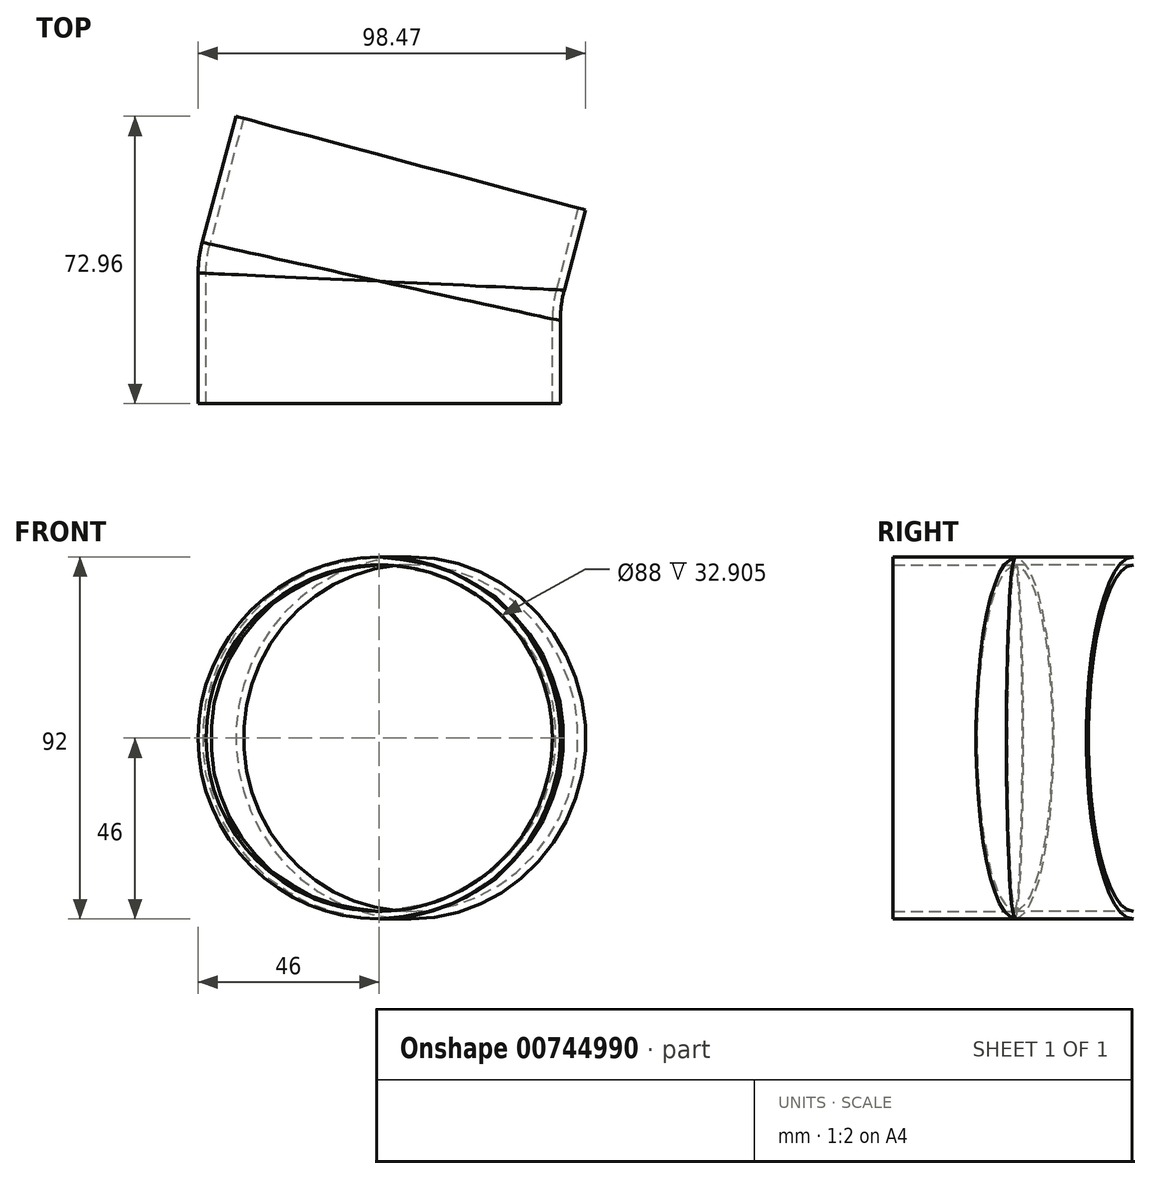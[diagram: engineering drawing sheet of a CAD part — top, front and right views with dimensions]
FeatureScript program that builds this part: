
annotation { "Feature Type Name" : "Feature", "Feature Type Description" : "" }
export const myFeature = defineFeature(function(context is Context, id is Id, definition is map)
    precondition{}
    {
        {
            var Q0;
            Q0=qCreatedBy(makeId("Front.planeOp"),FACE);
            var sketch = newSketch(context, id + "F0", { "sketchPlane" : qUnion([Q0])});
            skCircle(sketch, "E0", {"center": v(0, 0) * mm, "radius": 46 * mm});
            skSolve(sketch);
        }
        {
            var Q0;
            Q0=makeQuery(id+"F0.imprint","IMPRINT",FACE,{"disambiguationData":[TD([[makeQuery(id+"F0.imprint","IMPRINT",EDGE,{"derivedFrom":sQuery(id+"F0.wireOp",EDGE,"E0")}),1.0]])]});
            extrude(context, id + "F1", {"entities" : qUnion([Q0]), "depth" : 50 * mm, "offsetDistance" : 25 * mm});
        }
        {
            var Q0;
            Q0=qCreatedBy(makeId("Top.planeOp"),FACE);
            var sketch = newSketch(context, id + "F2", { "sketchPlane" : qUnion([Q0])});
            skLineSegment(sketch, "E1", {"start": v(0, 0) * mm, "end": v(46, 0) * mm, "construction": true});
            skLineSegment(sketch, "E2", {"start": v(46, 0) * mm, "end": v(-46, 0) * mm});
            skLineSegment(sketch, "E3", {"start": v(-46, 0) * mm, "end": v(-46, -12.89) * mm});
            skLineSegment(sketch, "E4", {"start": v(46, 0) * mm, "end": v(46, -25) * mm});
            skLineSegment(sketch, "E5", {"start": v(46, -25) * mm, "end": v(-46, -12.89) * mm});
            skSolve(sketch);
        }
        {
            var Q0;
            Q0 = qSketchRegion(id + "F2", true);
            extrude(context, id + "F3", {"entities" : qUnion([Q0]), "operationType" : NewBodyOperationType.REMOVE, "endBound" : BoundingType.THROUGH_ALL, "oppositeDirection" : true, "depth" : 25 * mm, "offsetDistance" : 25 * mm, "hasSecondDirection" : true, "secondDirectionBound" : SecondDirectionBoundingType.THROUGH_ALL, "secondDirectionOppositeDirection" : false, "secondDirectionDepth" : 25 * mm});
        }
        {
            var Q0;
            Q0=qCreatedBy(makeId("Front.planeOp"),FACE);
            var sketch = newSketch(context, id + "F4", { "sketchPlane" : qUnion([Q0])});
            skCircle(sketch, "E6", {"center": v(0, 0) * mm, "radius": 44 * mm});
            skSolve(sketch);
        }
        {
            var Q0;
            Q0 = qSketchRegion(id + "F4", true);
            extrude(context, id + "F5", {"entities" : qUnion([Q0]), "operationType" : NewBodyOperationType.REMOVE, "endBound" : BoundingType.THROUGH_ALL, "depth" : 25 * mm, "offsetDistance" : 25 * mm});
        }
        {
            var Q0;
            Q0=makeQuery(id+"F1.opExtrude","SWEPT_BODY",BODY,{"disambiguationData":[OSD([sQuery(id+"F0.wireOp",EDGE,"E0")])]});
            var Q1;
            Q1=makeQuery(id+"F3.boolean.opBoolean","COPY",FACE,{"derivedFrom":makeQuery(id+"F3.opExtrude","SWEPT_FACE",FACE,{"disambiguationData":[OSD([sQuery(id+"F2.wireOp",EDGE,"E5")])]})});
            mirror(context, id + "F6", {"operationType" : NewBodyOperationType.ADD, "entities" : qUnion([Q0]), "mirrorPlane" : qUnion([Q1])});
        }
        {
            var Q0;
            {var subQ0=makeQuery(id+"F5.boolean.opBoolean","INTERSECT",EDGE,{"derivedFrom":[makeQuery(id+"F3.boolean.opBoolean","COPY",FACE,{"derivedFrom":makeQuery(id+"F3.opExtrude","SWEPT_FACE",FACE,{"disambiguationData":[OSD([sQuery(id+"F2.wireOp",EDGE,"E5")])]})}),makeQuery(id+"F5.opExtrude","SWEPT_FACE",FACE,{"disambiguationData":[OSD([sQuery(id+"F4.wireOp",EDGE,"E6")])]})]});Q0=makeQuery(id+"F6.boolean.opBoolean","MERGE",EDGE,{"derivedFrom":[subQ0,makeQuery(id+"F6.opPattern","COPY",EDGE,{"derivedFrom":subQ0,"instanceName":"1"})]});}
            var Q1;
            {var subQ0=makeQuery(id+"F3.boolean.opBoolean","INTERSECT",EDGE,{"derivedFrom":[makeQuery(id+"F1.opExtrude","SWEPT_FACE",FACE,{"disambiguationData":[OSD([sQuery(id+"F0.wireOp",EDGE,"E0")])]}),makeQuery(id+"F3.opExtrude","SWEPT_FACE",FACE,{"disambiguationData":[OSD([sQuery(id+"F2.wireOp",EDGE,"E5")])]})]});Q1=makeQuery(id+"F6.boolean.opBoolean","MERGE",EDGE,{"derivedFrom":[subQ0,makeQuery(id+"F6.opPattern","COPY",EDGE,{"derivedFrom":subQ0,"instanceName":"1"})]});}
            fillet(context, id + "F7", {"entities" : qUnion([Q0, Q1]), "radius" : 30 * mm, "tangentPropagation" : true, "allowEdgeOverflow" : false});
        }
    });
